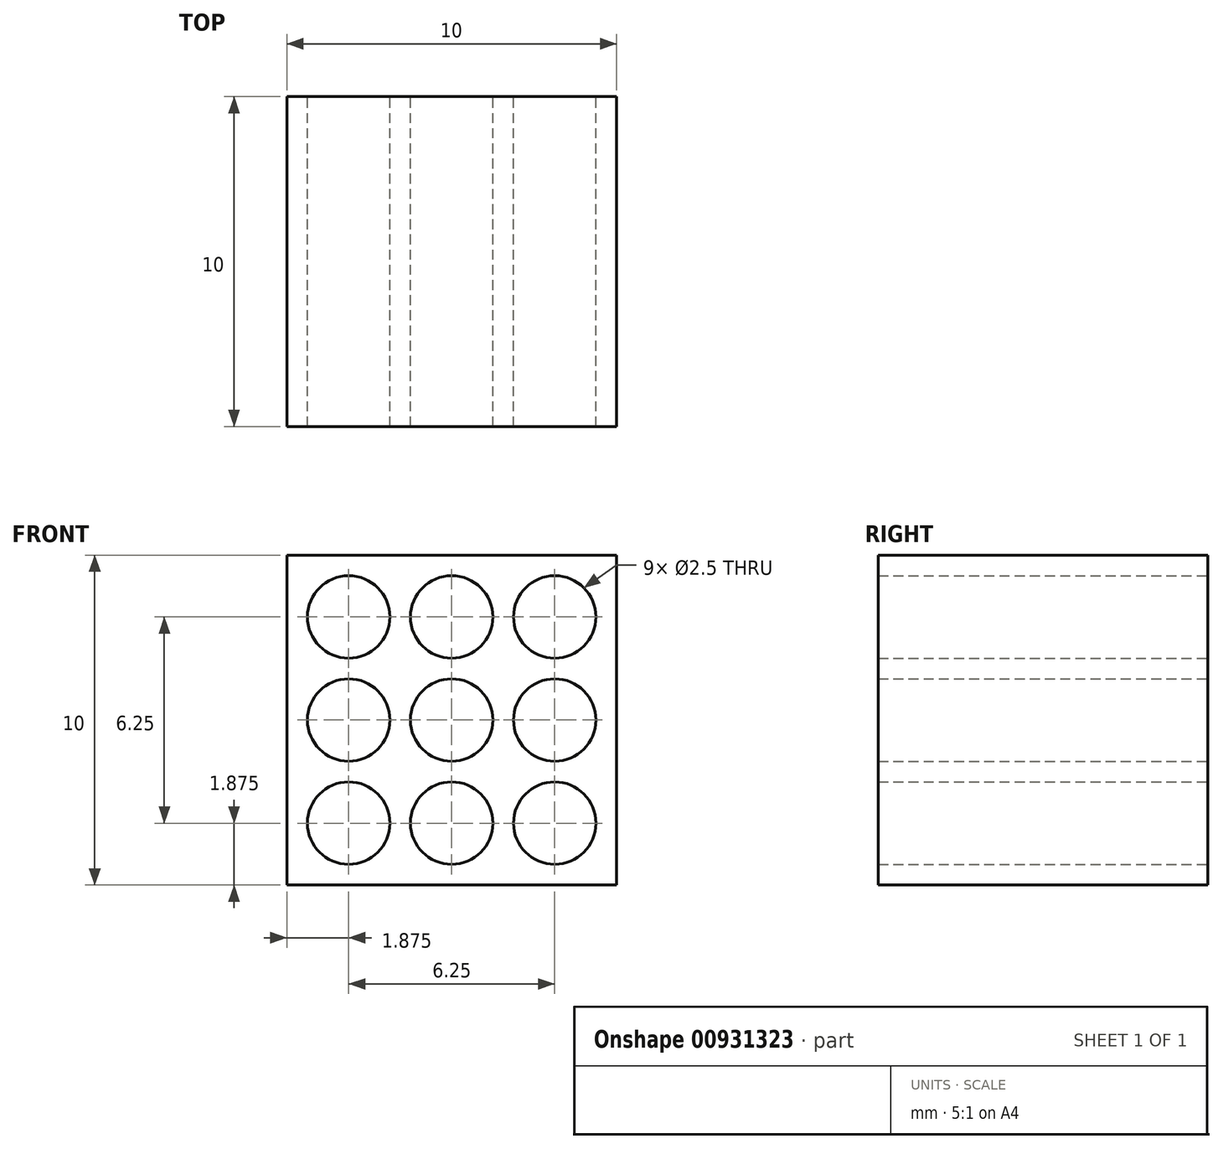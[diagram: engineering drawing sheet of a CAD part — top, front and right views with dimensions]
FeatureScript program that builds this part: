
annotation { "Feature Type Name" : "Feature", "Feature Type Description" : "" }
export const myFeature = defineFeature(function(context is Context, id is Id, definition is map)
    precondition{}
    {
        {
            var Q0;
            Q0=qCreatedBy(makeId("Front.planeOp"),FACE);
            var sketch = newSketch(context, id + "F0", { "sketchPlane" : qUnion([Q0])});
            skLineSegment(sketch, "E0.bottom", {"start": v(-5, 5) * mm, "end": v(5, 5) * mm});
            skLineSegment(sketch, "E0.top", {"start": v(-5, -5) * mm, "end": v(5, -5) * mm});
            skLineSegment(sketch, "E0.left", {"start": v(-5, 5) * mm, "end": v(-5, -5) * mm});
            skLineSegment(sketch, "E0.right", {"start": v(5, 5) * mm, "end": v(5, -5) * mm});
            skPoint(sketch, "E1", {"position": v(0, 0) * mm});
            skCircle(sketch, "E2", {"center": v(-3.12, 3.13) * mm, "radius": 1.25 * mm});
            skCircle(sketch, "E3", {"center": v(0, 3.13) * mm, "radius": 1.25 * mm});
            skCircle(sketch, "E4", {"center": v(3.13, 3.13) * mm, "radius": 1.25 * mm});
            skCircle(sketch, "E5", {"center": v(-3.12, 0) * mm, "radius": 1.25 * mm});
            skCircle(sketch, "E6", {"center": v(0, 0) * mm, "radius": 1.25 * mm});
            skCircle(sketch, "E7", {"center": v(3.13, 0) * mm, "radius": 1.25 * mm});
            skCircle(sketch, "E8", {"center": v(-3.13, -3.12) * mm, "radius": 1.25 * mm});
            skCircle(sketch, "E9", {"center": v(0, -3.12) * mm, "radius": 1.25 * mm});
            skCircle(sketch, "E10", {"center": v(3.13, -3.12) * mm, "radius": 1.25 * mm});
            skSolve(sketch);
        }
        {
            var Q0;
            Q0=makeQuery(id+"F0.imprint","IMPRINT",FACE,{"disambiguationData":[TD([[makeQuery(id+"F0.imprint","IMPRINT",EDGE,{"derivedFrom":sQuery(id+"F0.wireOp",EDGE,"E0.bottom")}),-1.0]])]});
            extrude(context, id + "F1", {"entities" : qUnion([Q0]), "depth" : 10 * mm, "offsetDistance" : 25.4 * mm});
        }
    });
